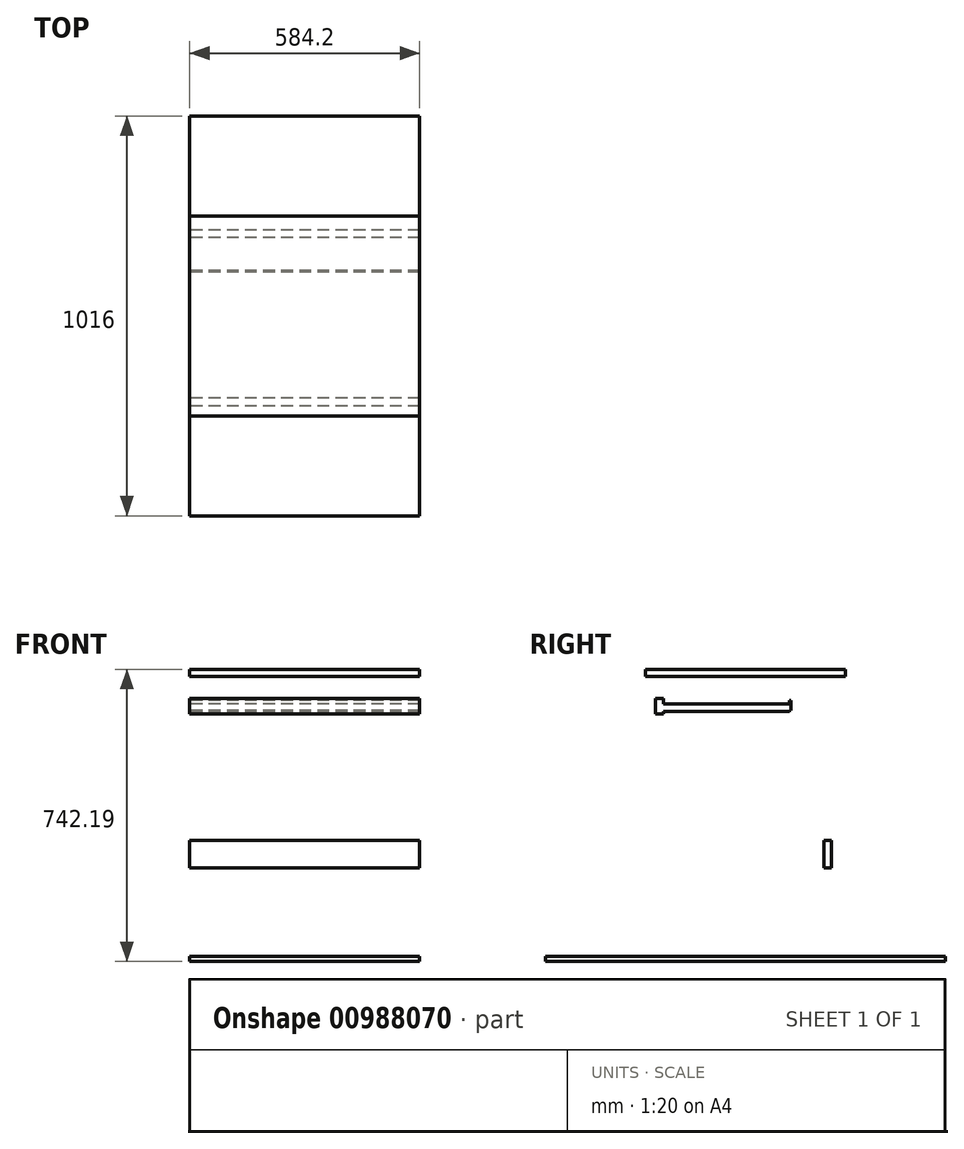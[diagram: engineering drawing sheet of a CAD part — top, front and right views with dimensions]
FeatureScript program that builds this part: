
annotation { "Feature Type Name" : "Feature", "Feature Type Description" : "" }
export const myFeature = defineFeature(function(context is Context, id is Id, definition is map)
    precondition{}
    {
        {
            var Q0;
            Q0=qCreatedBy(makeId("Right.planeOp"),FACE);
            var sketch = newSketch(context, id + "F0", { "sketchPlane" : qUnion([Q0])});
            skLineSegment(sketch, "E0.bottom", {"start": v(254, 0) * mm, "end": v(-254, 0) * mm});
            skLineSegment(sketch, "E0.top", {"start": v(254, 18.29) * mm, "end": v(-254, 18.29) * mm});
            skLineSegment(sketch, "E0.left", {"start": v(254, 0) * mm, "end": v(254, 18.29) * mm});
            skLineSegment(sketch, "E0.right", {"start": v(-254, 0) * mm, "end": v(-254, 18.29) * mm});
            skPoint(sketch, "E0.middle", {"position": v(0, 9.14) * mm});
            skLineSegment(sketch, "E1.bottom", {"start": v(218.44, 0) * mm, "end": v(198.63, 0) * mm});
            skLineSegment(sketch, "E1.top", {"start": v(218.44, -92.07) * mm, "end": v(198.63, -92.07) * mm});
            skLineSegment(sketch, "E1.left", {"start": v(218.44, 0) * mm, "end": v(218.44, -92.07) * mm});
            skLineSegment(sketch, "E1.right", {"start": v(198.63, 0) * mm, "end": v(198.63, -92.07) * mm});
            skLineSegment(sketch, "E2.bottom", {"start": v(198.63, -8.89) * mm, "end": v(173.23, -8.89) * mm});
            skLineSegment(sketch, "E2.top", {"start": v(198.63, -69.21) * mm, "end": v(173.23, -69.21) * mm});
            skLineSegment(sketch, "E2.left", {"start": v(198.63, -8.89) * mm, "end": v(198.63, -69.21) * mm});
            skLineSegment(sketch, "E2.right", {"start": v(173.23, -8.89) * mm, "end": v(173.23, -69.21) * mm});
            skLineSegment(sketch, "E3.bottom", {"start": v(198.63, -415.92) * mm, "end": v(218.44, -415.92) * mm});
            skLineSegment(sketch, "E3.top", {"start": v(198.63, -485.77) * mm, "end": v(218.44, -485.77) * mm});
            skLineSegment(sketch, "E3.left", {"start": v(198.63, -415.92) * mm, "end": v(198.63, -485.77) * mm});
            skLineSegment(sketch, "E3.right", {"start": v(218.44, -415.92) * mm, "end": v(218.44, -485.77) * mm});
            skLineSegment(sketch, "E4.bottom", {"start": v(111.63, -69.09) * mm, "end": v(-209.04, -69.09) * mm});
            skLineSegment(sketch, "E4.top", {"start": v(111.63, -88.9) * mm, "end": v(-209.04, -88.9) * mm});
            skLineSegment(sketch, "E4.left", {"start": v(111.63, -69.09) * mm, "end": v(111.63, -88.9) * mm});
            skLineSegment(sketch, "E4.right", {"start": v(-209.04, -69.09) * mm, "end": v(-209.04, -88.9) * mm});
            skLineSegment(sketch, "E5.bottom", {"start": v(-508, -711.2) * mm, "end": v(508, -711.2) * mm});
            skLineSegment(sketch, "E5.top", {"start": v(-508, -723.9) * mm, "end": v(508, -723.9) * mm});
            skLineSegment(sketch, "E5.left", {"start": v(-508, -711.2) * mm, "end": v(-508, -723.9) * mm});
            skLineSegment(sketch, "E5.right", {"start": v(508, -711.2) * mm, "end": v(508, -723.9) * mm});
            skPoint(sketch, "E6", {"position": v(0, -711.2) * mm});
            skLineSegment(sketch, "E7.bottom", {"start": v(-228.6, -55.88) * mm, "end": v(-209.04, -55.88) * mm});
            skLineSegment(sketch, "E7.top", {"start": v(-228.6, -95.25) * mm, "end": v(-209.04, -95.25) * mm});
            skLineSegment(sketch, "E7.left", {"start": v(-228.6, -55.88) * mm, "end": v(-228.6, -95.25) * mm});
            skLineSegment(sketch, "E7.right", {"start": v(-209.04, -55.88) * mm, "end": v(-209.04, -95.25) * mm});
            skLineSegment(sketch, "E8.bottom", {"start": v(111.63, -85.72) * mm, "end": v(114.8, -85.72) * mm});
            skLineSegment(sketch, "E8.top", {"start": v(111.63, -60.32) * mm, "end": v(114.8, -60.32) * mm});
            skLineSegment(sketch, "E8.left", {"start": v(111.63, -85.72) * mm, "end": v(111.63, -60.32) * mm});
            skLineSegment(sketch, "E8.right", {"start": v(114.8, -85.72) * mm, "end": v(114.8, -60.32) * mm});
            skSolve(sketch);
        }
        {
            var Q0;
            Q0=makeQuery(id+"F0.imprint","IMPRINT",FACE,{"disambiguationData":[TD([[makeQuery(id+"F0.imprint","IMPRINT",EDGE,{"derivedFrom":sQuery(id+"F0.wireOp",EDGE,"E3.bottom")}),-1.0]])]});
            var Q1;
            Q1=makeQuery(id+"F0.imprint","IMPRINT",FACE,{"disambiguationData":[TD([[makeQuery(id+"F0.imprint","IMPRINT",EDGE,{"derivedFrom":sQuery(id+"F0.wireOp",EDGE,"E4.bottom")}),1.0]])]});
            var Q2;
            Q2=makeQuery(id+"F0.imprint","IMPRINT",FACE,{"disambiguationData":[TD([[makeQuery(id+"F0.imprint","IMPRINT",EDGE,{"derivedFrom":sQuery(id+"F0.wireOp",EDGE,"E5.bottom")}),-1.0]])]});
            var Q3;
            Q3=makeQuery(id+"F0.imprint","IMPRINT",FACE,{"disambiguationData":[TD([[makeQuery(id+"F0.imprint","IMPRINT",EDGE,{"derivedFrom":sQuery(id+"F0.wireOp",EDGE,"E0.top")}),1.0]])]});
            var Q4;
            {var subQ1=sQuery(id+"F0.wireOp",EDGE,"E1.bottom");Q4=makeQuery(id+"F0.imprint","IMPRINT",FACE,{"disambiguationData":[TD([[makeQuery(id+"F0.imprint","IMPRINT",EDGE,{"derivedFrom":subQ1}),1.0]])]});}
            var Q5;
            {var subQ2=sQuery(id+"F0.wireOp",EDGE,"E7.bottom");Q5=makeQuery(id+"F0.imprint","IMPRINT",FACE,{"disambiguationData":[TD([[makeQuery(id+"F0.imprint","IMPRINT",EDGE,{"derivedFrom":subQ2}),-1.0]])]});}
            var Q6;
            {var subQ3=sQuery(id+"F0.wireOp",EDGE,"E8.bottom");Q6=makeQuery(id+"F0.imprint","IMPRINT",FACE,{"disambiguationData":[TD([[makeQuery(id+"F0.imprint","IMPRINT",EDGE,{"derivedFrom":subQ3}),1.0]])]});}
            extrude(context, id + "F1", {"entities" : qUnion([Q0, Q1, Q2, Q3, Q4, Q5, Q6]), "endBound" : BoundingType.SYMMETRIC, "depth" : 584.2 * mm, "offsetDistance" : 25.4 * mm});
        }
    });
